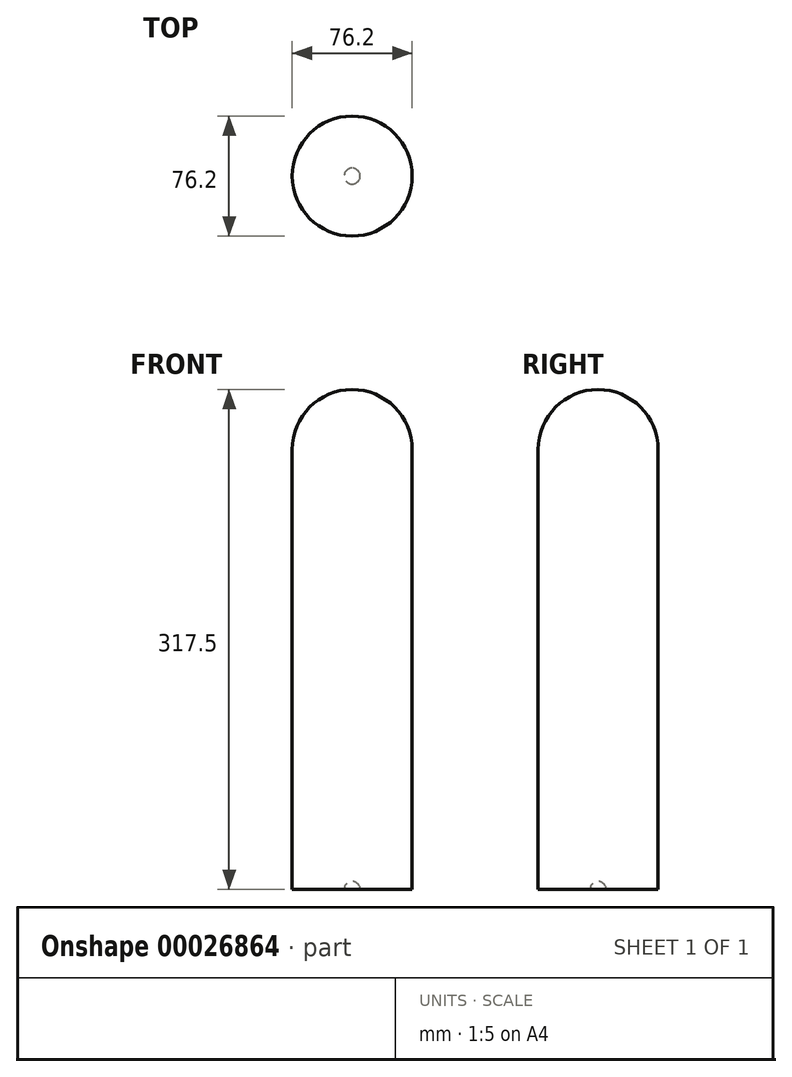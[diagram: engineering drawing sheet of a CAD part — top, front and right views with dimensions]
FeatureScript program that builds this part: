
annotation { "Feature Type Name" : "Feature", "Feature Type Description" : "" }
export const myFeature = defineFeature(function(context is Context, id is Id, definition is map)
    precondition{}
    {
        {
            var Q0;
            Q0=qCreatedBy(makeId("Top.planeOp"),FACE);
            var sketch = newSketch(context, id + "F0", { "sketchPlane" : qUnion([Q0])});
            skCircle(sketch, "E0", {"center": v(0, 0) * mm, "radius": 38.1 * mm});
            skSolve(sketch);
        }
        {
            var Q0;
            Q0=makeQuery(id+"F0.imprint","IMPRINT",FACE,{"disambiguationData":[TD([[makeQuery(id+"F0.imprint","IMPRINT",EDGE,{"derivedFrom":sQuery(id+"F0.wireOp",EDGE,"E0")}),1.0]])]});
            extrude(context, id + "F1", {"entities" : qUnion([Q0]), "depth" : 279.4 * mm});
        }
        {
            var Q0;
            Q0=makeQuery(id+"F1.opExtrude","CAP_FACE",FACE,{"disambiguationData":[OSD([sQuery(id+"F0.wireOp",EDGE,"E0")])],"isStart":false});
            var sketch = newSketch(context, id + "F2", { "sketchPlane" : qUnion([Q0])});
            skLineSegment(sketch, "E1", {"start": v(0, -38.1) * mm, "end": v(0, 38.1) * mm});
            skSolve(sketch);
        }
        {
            var Q0;
            {var subQ1=sQuery(id+"F2.wireOp",EDGE,"E1");Q0=makeQuery(id+"F2.imprint","IMPRINT",FACE,{"disambiguationData":[TD([[makeQuery(id+"F2.imprint","IMPRINT",EDGE,{"derivedFrom":subQ1}),-1.0]])]});}
            var Q1;
            Q1=sQuery(id+"F2.wireOp",EDGE,"E1");
            revolve(context, id + "F3", {"operationType" : NewBodyOperationType.ADD, "entities" : qUnion([Q0]), "axis" : qUnion([Q1]), "revolveType" : RevolveType.FULL});
        }
        {
            var Q0;
            Q0=makeQuery(id+"F1.opExtrude","CAP_FACE",FACE,{"disambiguationData":[OSD([sQuery(id+"F0.wireOp",EDGE,"E0")])],"isStart":true});
            var sketch = newSketch(context, id + "F4", { "sketchPlane" : qUnion([Q0])});
            skCircle(sketch, "E2", {"center": v(0, 0) * mm, "radius": 5.08 * mm});
            skLineSegment(sketch, "E3", {"start": v(0, -5.08) * mm, "end": v(0, 5.08) * mm});
            skSolve(sketch);
        }
        {
            var Q0;
            {var subQ0=sQuery(id+"F4.wireOp",EDGE,"E3");Q0=makeQuery(id+"F4.imprint","IMPRINT",FACE,{"disambiguationData":[TD([[makeQuery(id+"F4.imprint","IMPRINT",EDGE,{"derivedFrom":subQ0}),-1.0]])]});}
            var Q1;
            Q1=sQuery(id+"F4.wireOp",EDGE,"E3");
            revolve(context, id + "F5", {"operationType" : NewBodyOperationType.REMOVE, "entities" : qUnion([Q0]), "axis" : qUnion([Q1]), "revolveType" : RevolveType.ONE_DIRECTION, "angle" : 180 * degree});
        }
    });
